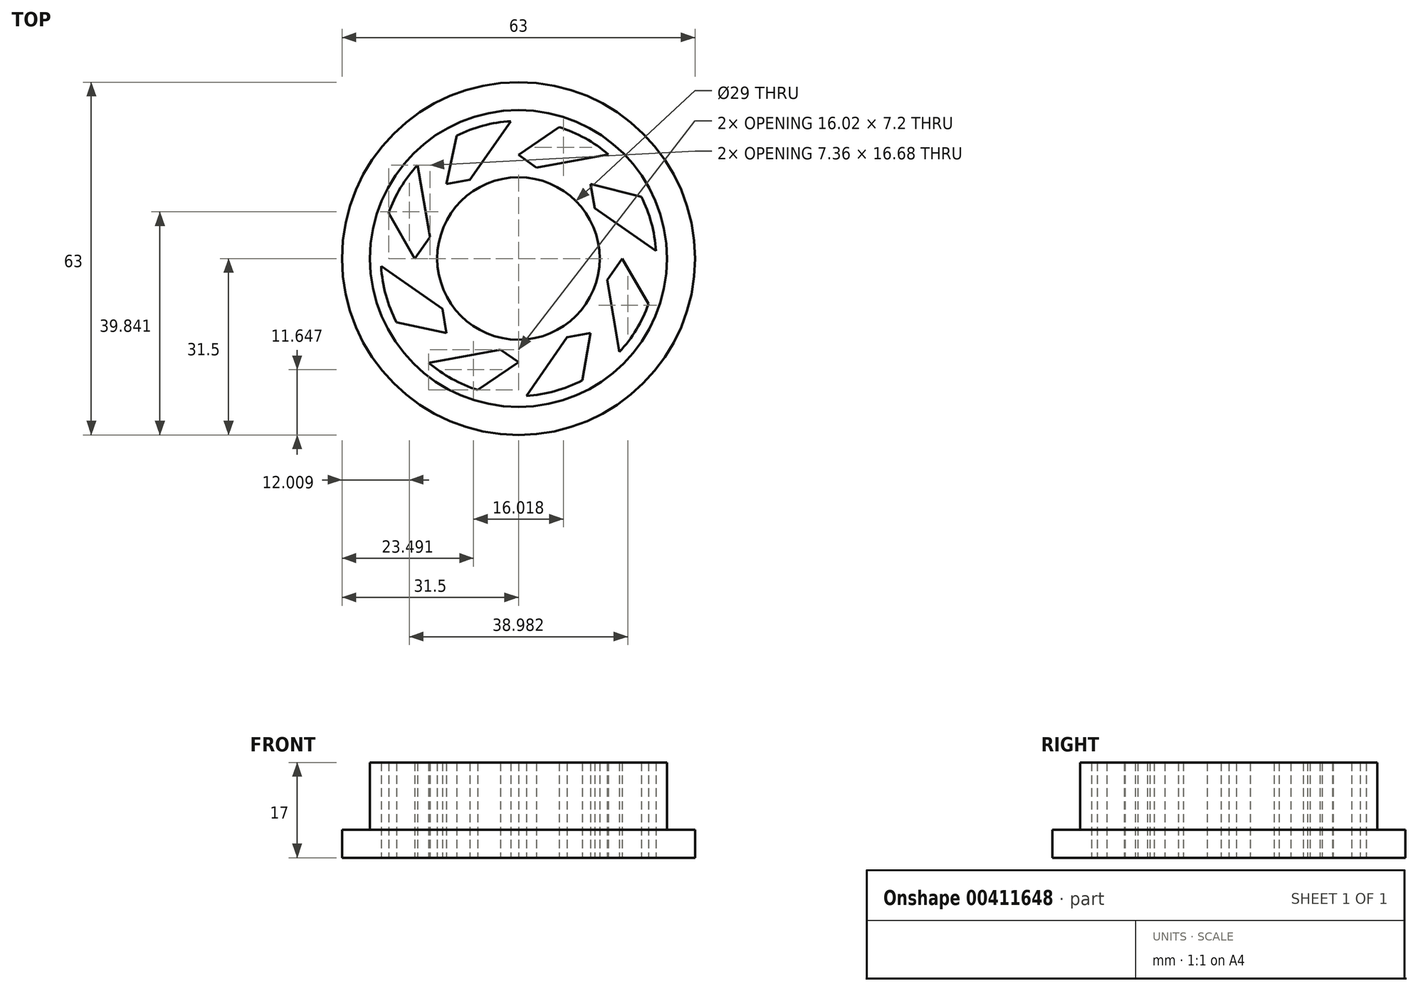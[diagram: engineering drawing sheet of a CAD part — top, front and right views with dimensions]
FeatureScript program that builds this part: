
annotation { "Feature Type Name" : "Feature", "Feature Type Description" : "" }
export const myFeature = defineFeature(function(context is Context, id is Id, definition is map)
    precondition{}
    {
        {
            var Q0;
            Q0=qCreatedBy(makeId("Top.planeOp"),FACE);
            var sketch = newSketch(context, id + "F0", { "sketchPlane" : qUnion([Q0])});
            skCircle(sketch, "E0", {"center": v(0, 0) * mm, "radius": 14.5 * mm});
            skCircle(sketch, "E1", {"center": v(0, 0) * mm, "radius": 31.5 * mm});
            skCircle(sketch, "E2", {"center": v(0, 0) * mm, "radius": 26.5 * mm});
            skLineSegment(sketch, "E3", {"start": v(18.5, 0) * mm, "end": v(15.8, -3.85) * mm});
            skLineSegment(sketch, "E4", {"start": v(12.86, -13.3) * mm, "end": v(8.68, -14.07) * mm});
            skLineSegment(sketch, "E5", {"start": v(-12.86, -13.3) * mm, "end": v(-13.6, -9) * mm});
            skLineSegment(sketch, "E6", {"start": v(-12.86, 13.3) * mm, "end": v(-8.68, 14.07) * mm});
            skLineSegment(sketch, "E7", {"start": v(12.86, 13.3) * mm, "end": v(13.6, 9) * mm});
            skLineSegment(sketch, "E8", {"start": v(0, -18.5) * mm, "end": v(-3.22, -16.25) * mm});
            skLineSegment(sketch, "E9", {"start": v(-18.5, 0) * mm, "end": v(-15.8, 3.85) * mm});
            skLineSegment(sketch, "E10", {"start": v(0, 18.5) * mm, "end": v(3.22, 16.25) * mm});
            skLineSegment(sketch, "E11.trimOffspring", {"start": v(8.68, -14.07) * mm, "end": v(1.39, -24.51) * mm});
            skLineSegment(sketch, "E12.trimOffspring", {"start": v(-13.6, -9) * mm, "end": v(-24.51, -1.39) * mm});
            skLineSegment(sketch, "E13.trimOffspring", {"start": v(-15.8, 3.85) * mm, "end": v(-18.01, 16.68) * mm});
            skLineSegment(sketch, "E14.trimOffspring", {"start": v(-8.68, 14.07) * mm, "end": v(-1.39, 24.51) * mm});
            skLineSegment(sketch, "E15.trimOffspring", {"start": v(3.22, 16.25) * mm, "end": v(16.02, 18.6) * mm});
            skLineSegment(sketch, "E16.trimOffspring", {"start": v(13.6, 9) * mm, "end": v(24.51, 1.39) * mm});
            skLineSegment(sketch, "E17.trimOffspring", {"start": v(15.8, -3.85) * mm, "end": v(18.01, -16.68) * mm});
            skLineSegment(sketch, "E18.trimOffspring", {"start": v(-3.22, -16.25) * mm, "end": v(-16.02, -18.6) * mm});
            skLineSegment(sketch, "E19", {"start": v(0, -18.5) * mm, "end": v(-7.27, -23.45) * mm});
            skLineSegment(sketch, "E20", {"start": v(-12.86, -13.3) * mm, "end": v(-21.75, -11.39) * mm});
            skLineSegment(sketch, "E21", {"start": v(-18.5, 0) * mm, "end": v(-23.17, 8.12) * mm});
            skLineSegment(sketch, "E22", {"start": v(-12.86, 13.3) * mm, "end": v(-11.05, 21.93) * mm});
            skLineSegment(sketch, "E23", {"start": v(0, 18.5) * mm, "end": v(7.27, 23.45) * mm});
            skLineSegment(sketch, "E24", {"start": v(18.5, 0) * mm, "end": v(23.17, -8.12) * mm});
            skArc(sketch, "E25", {"start": v(1.39, -24.51) * mm, "mid": v(6.53, -23.67) * mm, "end": v(11.39, -21.75) * mm});
            skPoint(sketch, "E26.orphan", {"position": v(0, -26.5) * mm});
            skPoint(sketch, "E27.orphan", {"position": v(-26.5, 0) * mm});
            skPoint(sketch, "E28.orphan", {"position": v(0, 26.5) * mm});
            skPoint(sketch, "E29.orphan", {"position": v(26.5, 0) * mm});
            skPoint(sketch, "E30.orphan", {"position": v(24.42, -10.29) * mm});
            skPoint(sketch, "E31.orphan", {"position": v(18.42, -19.05) * mm});
            skLineSegment(sketch, "E32", {"start": v(12.86, -13.3) * mm, "end": v(11.39, -21.75) * mm});
            skLineSegment(sketch, "E33", {"start": v(12.86, 13.3) * mm, "end": v(21.93, 11.05) * mm});
            skArc(sketch, "E34.trimOffspring", {"start": v(-16.02, -18.6) * mm, "mid": v(-11.9, -21.48) * mm, "end": v(-7.27, -23.45) * mm});
            skArc(sketch, "E35.trimOffspring", {"start": v(-24.51, -1.39) * mm, "mid": v(-23.67, -6.53) * mm, "end": v(-21.75, -11.39) * mm});
            skArc(sketch, "E36.trimOffspring", {"start": v(-18.01, 16.68) * mm, "mid": v(-21.03, 12.66) * mm, "end": v(-23.17, 8.12) * mm});
            skArc(sketch, "E37.trimOffspring", {"start": v(-1.39, 24.51) * mm, "mid": v(-6.35, 23.72) * mm, "end": v(-11.05, 21.93) * mm});
            skArc(sketch, "E38.trimOffspring", {"start": v(16.02, 18.6) * mm, "mid": v(11.9, 21.48) * mm, "end": v(7.27, 23.45) * mm});
            skArc(sketch, "E39.trimOffspring", {"start": v(24.51, 1.39) * mm, "mid": v(23.72, 6.35) * mm, "end": v(21.93, 11.05) * mm});
            skArc(sketch, "E40.trimOffspring", {"start": v(18.01, -16.68) * mm, "mid": v(21.03, -12.66) * mm, "end": v(23.17, -8.12) * mm});
            skSolve(sketch);
        }
        {
            var Q0;
            Q0=makeQuery(id+"F0.imprint","IMPRINT",FACE,{"disambiguationData":[TD([[makeQuery(id+"F0.imprint","IMPRINT",EDGE,{"derivedFrom":sQuery(id+"F0.wireOp",EDGE,"E0")}),-1.0]])]});
            extrude(context, id + "F1", {"entities" : qUnion([Q0]), "depth" : 17 * mm});
        }
        {
            var Q0;
            Q0=makeQuery(id+"F0.imprint","IMPRINT",FACE,{"disambiguationData":[TD([[makeQuery(id+"F0.imprint","IMPRINT",EDGE,{"derivedFrom":sQuery(id+"F0.wireOp",EDGE,"E1")}),1.0]])]});
            extrude(context, id + "F2", {"entities" : qUnion([Q0]), "operationType" : NewBodyOperationType.ADD, "depth" : 5 * mm});
        }
        {
            var Q0;
            Q0=makeQuery(id+"F0.imprint","IMPRINT",FACE,{"disambiguationData":[TD([[makeQuery(id+"F0.imprint","IMPRINT",EDGE,{"derivedFrom":sQuery(id+"F0.wireOp",EDGE,"E3")}),1.0]])]});
            var Q1;
            Q1=makeQuery(id+"F0.imprint","IMPRINT",FACE,{"disambiguationData":[TD([[makeQuery(id+"F0.imprint","IMPRINT",EDGE,{"derivedFrom":sQuery(id+"F0.wireOp",EDGE,"E4")}),1.0]])]});
            var Q2;
            Q2=makeQuery(id+"F0.imprint","IMPRINT",FACE,{"disambiguationData":[TD([[makeQuery(id+"F0.imprint","IMPRINT",EDGE,{"derivedFrom":sQuery(id+"F0.wireOp",EDGE,"E8")}),1.0]])]});
            var Q3;
            Q3=makeQuery(id+"F0.imprint","IMPRINT",FACE,{"disambiguationData":[TD([[makeQuery(id+"F0.imprint","IMPRINT",EDGE,{"derivedFrom":sQuery(id+"F0.wireOp",EDGE,"E5")}),1.0]])]});
            var Q4;
            Q4=makeQuery(id+"F0.imprint","IMPRINT",FACE,{"disambiguationData":[TD([[makeQuery(id+"F0.imprint","IMPRINT",EDGE,{"derivedFrom":sQuery(id+"F0.wireOp",EDGE,"E9")}),1.0]])]});
            var Q5;
            Q5=makeQuery(id+"F0.imprint","IMPRINT",FACE,{"disambiguationData":[TD([[makeQuery(id+"F0.imprint","IMPRINT",EDGE,{"derivedFrom":sQuery(id+"F0.wireOp",EDGE,"E6")}),1.0]])]});
            var Q6;
            Q6=makeQuery(id+"F0.imprint","IMPRINT",FACE,{"disambiguationData":[TD([[makeQuery(id+"F0.imprint","IMPRINT",EDGE,{"derivedFrom":sQuery(id+"F0.wireOp",EDGE,"E10")}),1.0]])]});
            var Q7;
            Q7=makeQuery(id+"F0.imprint","IMPRINT",FACE,{"disambiguationData":[TD([[makeQuery(id+"F0.imprint","IMPRINT",EDGE,{"derivedFrom":sQuery(id+"F0.wireOp",EDGE,"E7")}),1.0]])]});
            extrude(context, id + "F3", {"entities" : qUnion([Q0, Q1, Q2, Q3, Q4, Q5, Q6, Q7]), "operationType" : NewBodyOperationType.REMOVE, "depth" : 17 * mm});
        }
    });
